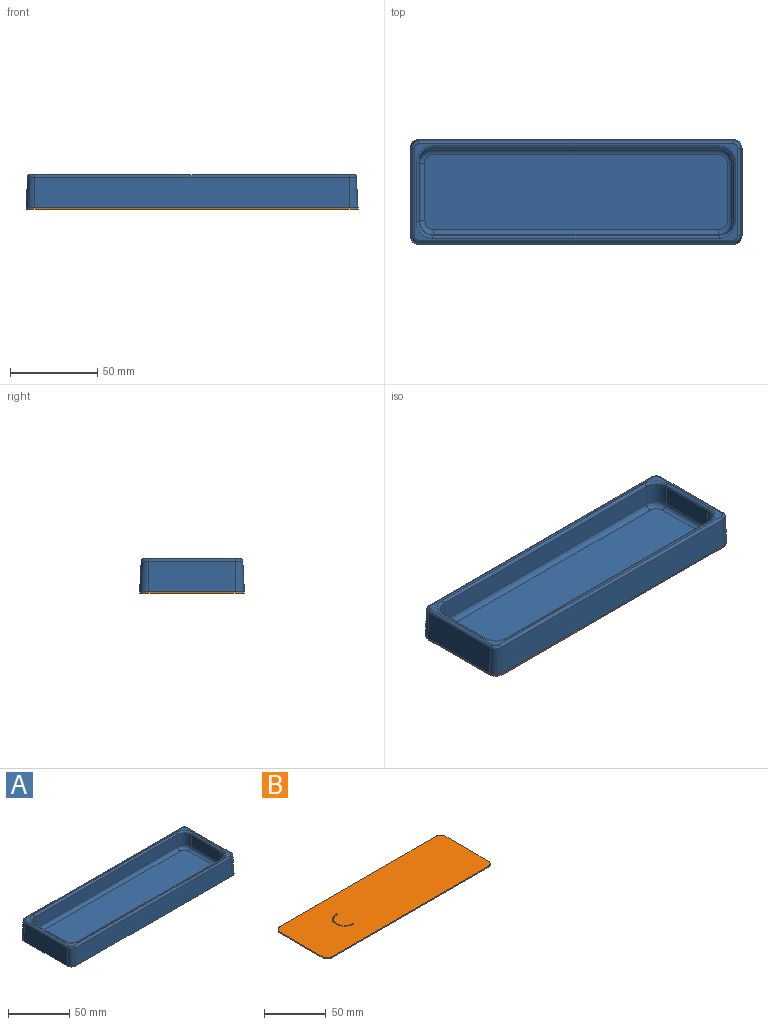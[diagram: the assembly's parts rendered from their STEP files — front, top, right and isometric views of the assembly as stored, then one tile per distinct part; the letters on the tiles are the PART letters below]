
ASSEMBLY  parts=2 mates=1
PART A: 69 faces, bbox 190x60x19 mm
  f0: plane 190x60mm, normal (0,0,-1), area 731mm2, adj f2,f3,f4,f5,f6,f7,f8,f9
  f1: plane 185.16x55.16mm, normal (0,0,1), area 610.7mm2, adj f19,f20,f21,f22,f23,f24,f25,f26
  f2: plane 180x17.58mm, normal (0,1,0.05), area 3168.5mm2, adj f0,f3,f9,f30
  f3: cone r=5mm half-angle=3deg, axis (0,0,-1), area 125.5mm2, adj f0,f2,f4,f32
  f4: plane 50x17.58mm, normal (-1,0,0.05), area 880.1mm2, adj f0,f3,f5,f34
  f5: cone r=5mm half-angle=3deg, axis (0,0,-1), area 125.5mm2, adj f0,f4,f6,f33
  f6: plane 180x17.58mm, normal (0,-1,0.05), area 3168.5mm2, adj f0,f5,f7,f31
  f7: cone r=5mm half-angle=3deg, axis (0,0,-1), area 125.5mm2, adj f0,f6,f8,f29
  f8: plane 50x17.58mm, normal (1,0,0.05), area 880.1mm2, adj f0,f7,f9,f27
  f9: cone r=5mm half-angle=3deg, axis (0,0,-1), area 125.5mm2, adj f0,f2,f8,f28
  f10: plane 163.91x11.66mm, normal (0,-1,0.03), area 1907.1mm2, adj f15,f18,f22,f42
  f11: plane 33.91x11.66mm, normal (1,0,0.03), area 390.8mm2, adj f15,f16,f26,f38
  f12: plane 163.91x11.66mm, normal (0,1,0.03), area 1907.1mm2, adj f16,f17,f23,f35
  f13: plane 33.91x11.66mm, normal (-1,0,0.03), area 390.8mm2, adj f17,f18,f19,f39
  f14: plane 173.09x43.09mm, normal (0,0,1), area 7436.7mm2, adj f35,f36,f37,f38,f39,f40,f41,f42
  f15: cylinder r=8mm len=11.91mm, axis (0.03,-0.03,-1), area 147.1mm2, adj f10,f11,f24,f40
  f16: cylinder r=8mm len=11.91mm, axis (0.03,0.03,-1), area 147.1mm2, adj f11,f12,f25,f36
  f17: cylinder r=8mm len=11.91mm, axis (-0.03,0.03,-1), area 147.1mm2, adj f12,f13,f21,f37
  f18: cylinder r=8mm len=11.91mm, axis (-0.03,-0.03,-1), area 147.1mm2, adj f10,f13,f20,f41
  f19: cylinder r=1.5mm len=33.91mm, axis (0,1,0), area 78.1mm2, adj f1,f13,f20,f21
  f20: bspline ~9.49x9.49mm, area 30.8mm2, adj f1,f18,f19,f22
  f21: bspline ~9.49x9.49mm, area 30.8mm2, adj f1,f17,f19,f23
  f22: cylinder r=1.5mm len=163.91mm, axis (-1,0,0), area 377.6mm2, adj f1,f10,f20,f24
  f23: cylinder r=1.5mm len=163.91mm, axis (-1,0,0), area 377.6mm2, adj f1,f12,f21,f25
  f24: bspline ~9.49x9.49mm, area 30.8mm2, adj f1,f15,f22,f26
  f25: bspline ~9.49x9.49mm, area 30.8mm2, adj f1,f16,f23,f26
  f26: cylinder r=1.5mm len=33.91mm, axis (0,1,0), area 78.1mm2, adj f1,f11,f24,f25
  f27: cylinder r=1.5mm len=50mm, axis (0,-1,0), area 113.9mm2, adj f1,f8,f28,f29
  f28: torus R=2.58mm, axis (0,0,1), area 12.6mm2, adj f1,f9,f27,f30
  f29: torus R=2.58mm, axis (0,0,1), area 12.6mm2, adj f1,f7,f27,f31
  f30: cylinder r=1.5mm len=180mm, axis (1,0,0), area 410mm2, adj f1,f2,f28,f32
  f31: cylinder r=1.5mm len=180mm, axis (1,0,0), area 410mm2, adj f1,f6,f29,f33
  f32: torus R=2.58mm, axis (0,0,1), area 12.6mm2, adj f1,f3,f30,f34
  f33: torus R=2.58mm, axis (0,0,1), area 12.6mm2, adj f1,f5,f31,f34
  f34: cylinder r=1.5mm len=50mm, axis (0,-1,0), area 113.9mm2, adj f1,f4,f32,f33
  f35: cylinder r=3mm len=163.09mm, axis (1,0,0), area 751.5mm2, adj f12,f14,f36,f37
  f36: bspline ~8.35x8.35mm, area 49.5mm2, adj f14,f16,f35,f38
  f37: bspline ~8.35x8.35mm, area 49.5mm2, adj f14,f17,f35,f39
  f38: cylinder r=3mm len=33.09mm, axis (0,-1,0), area 152.5mm2, adj f11,f14,f36,f40
  f39: cylinder r=3mm len=33.09mm, axis (0,-1,0), area 152.5mm2, adj f13,f14,f37,f41
  f40: bspline ~8.35x8.35mm, area 49.5mm2, adj f14,f15,f38,f42
  f41: bspline ~8.35x8.35mm, area 49.5mm2, adj f14,f18,f39,f42
  f42: cylinder r=3mm len=163.09mm, axis (1,0,0), area 751.5mm2, adj f10,f14,f40,f41
  f43: plane 185.16x55.16mm, normal (0,0,-1), area 610.7mm2, adj f44,f45,f46,f47,f48,f49,f50,f51
  f44: plane 180x17.5mm, normal (0,-1,-0.05), area 3154.3mm2, adj f0,f43,f45,f51
  f45: cone r=3.5mm half-angle=3deg, axis (0,0,-1), area 83.7mm2, adj f0,f43,f44,f46
  f46: plane 50x17.5mm, normal (1,0,-0.05), area 876.2mm2, adj f0,f43,f45,f47
  f47: cone r=3.5mm half-angle=3deg, axis (0,0,-1), area 83.7mm2, adj f0,f43,f46,f48
  f48: plane 180x17.5mm, normal (0,1,-0.05), area 3154.3mm2, adj f0,f43,f47,f49
  f49: cone r=3.5mm half-angle=3deg, axis (0,0,-1), area 83.7mm2, adj f0,f43,f48,f50
  f50: plane 50x17.5mm, normal (-1,0,-0.05), area 876.2mm2, adj f0,f43,f49,f51
  f51: cone r=3.5mm half-angle=3deg, axis (0,0,-1), area 83.7mm2, adj f0,f43,f44,f50
  f52: plane 163.91x11.66mm, normal (0,1,-0.03), area 1907.1mm2, adj f43,f57,f60,f68
  f53: plane 33.91x11.66mm, normal (-1,0,-0.03), area 390.8mm2, adj f43,f57,f58,f64
  f54: plane 163.91x11.66mm, normal (0,-1,-0.03), area 1907.1mm2, adj f43,f58,f59,f61
  f55: plane 33.91x11.66mm, normal (1,0,-0.03), area 390.8mm2, adj f43,f59,f60,f65
  f56: plane 173.09x43.09mm, normal (0,0,-1), area 7436.7mm2, adj f61,f62,f63,f64,f65,f66,f67,f68
  f57: cylinder r=9.5mm len=11.93mm, axis (0.03,-0.03,-1), area 174.7mm2, adj f43,f52,f53,f66
  f58: cylinder r=9.5mm len=11.93mm, axis (0.03,0.03,-1), area 174.7mm2, adj f43,f53,f54,f62
  f59: cylinder r=9.5mm len=11.93mm, axis (-0.03,0.03,-1), area 174.7mm2, adj f43,f54,f55,f63
  f60: cylinder r=9.5mm len=11.93mm, axis (-0.03,-0.03,-1), area 174.7mm2, adj f43,f52,f55,f67
  f61: cylinder r=4.5mm len=163.09mm, axis (1,0,0), area 1127.2mm2, adj f54,f56,f62,f63
  f62: bspline ~9.49x9.49mm, area 84.3mm2, adj f56,f58,f61,f64
  f63: bspline ~9.49x9.49mm, area 84.3mm2, adj f56,f59,f61,f65
  f64: cylinder r=4.5mm len=33.09mm, axis (0,-1,0), area 228.7mm2, adj f53,f56,f62,f66
  f65: cylinder r=4.5mm len=33.09mm, axis (0,-1,0), area 228.7mm2, adj f55,f56,f63,f67
  f66: bspline ~9.49x9.49mm, area 84.3mm2, adj f56,f57,f64,f68
  f67: bspline ~9.49x9.49mm, area 84.3mm2, adj f56,f60,f65,f68
  f68: cylinder r=4.5mm len=163.09mm, axis (1,0,0), area 1127.2mm2, adj f52,f56,f66,f67
PART B: 14 faces, bbox 190x60x1 mm
  f0: plane 178x1mm, normal (0,-1,0), area 178mm2, adj f1,f11,f12,f13
  f1: cylinder r=6mm len=6mm, axis (0,0,-1), area 9.4mm2, adj f0,f2,f12,f13
  f2: plane 48x1mm, normal (1,0,0), area 48mm2, adj f1,f3,f12,f13
  f3: cylinder r=6mm len=6mm, axis (0,0,-1), area 9.4mm2, adj f2,f4,f12,f13
  f4: plane 178x1mm, normal (0,1,0), area 178mm2, adj f3,f5,f12,f13
  f5: cylinder r=6mm len=6mm, axis (0,0,-1), area 9.4mm2, adj f4,f6,f12,f13
  f6: plane 48x1mm, normal (-1,0,0), area 48mm2, adj f5,f11,f12,f13
  f7: cylinder r=0.5mm len=1mm, axis (0,0,-1), area 1.6mm2, adj f8,f10,f12,f13
  f8: cylinder r=9mm len=18mm, axis (0,0,-1), area 28.6mm2, adj f7,f9,f12,f13
  f9: cylinder r=0.5mm len=1mm, axis (0,0,-1), area 1.6mm2, adj f8,f10,f12,f13
  f10: cylinder r=10mm len=20mm, axis (0,0,-1), area 31.8mm2, adj f7,f9,f12,f13
  f11: cylinder r=6mm len=6mm, axis (0,0,-1), area 9.4mm2, adj f0,f6,f12,f13
  f12: plane 190x60mm, normal (0,0,1), area 11338.1mm2, adj f0,f1,f2,f3,f4,f5,f6,f7
  f13: plane 190x60mm, normal (0,0,-1), area 11338.1mm2, adj f0,f1,f2,f3,f4,f5,f6,f7
PLACE A t=(24.35,49.57,-15.45)mm
PLACE B t=(24.35,49.57,-16.45)mm
MATE fastened A.f0 <-> B.f12  axis (0,0,-1) through (119.35,49.57,-15.45)mm
